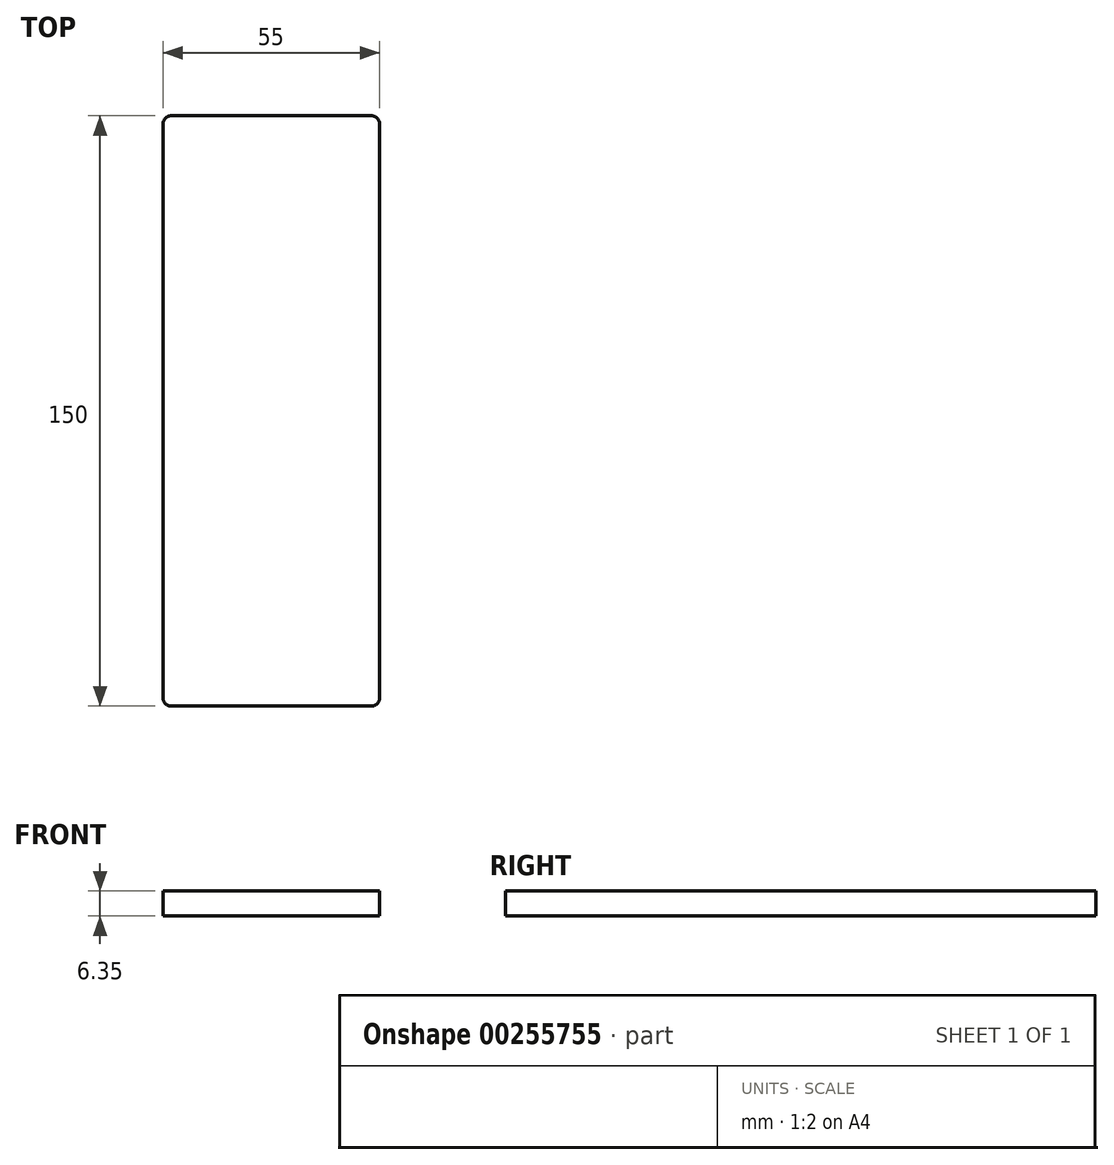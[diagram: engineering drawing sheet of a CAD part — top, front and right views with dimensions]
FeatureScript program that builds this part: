
annotation { "Feature Type Name" : "Feature", "Feature Type Description" : "" }
export const myFeature = defineFeature(function(context is Context, id is Id, definition is map)
    precondition{}
    {
        {
            var Q0;
            Q0=qCreatedBy(makeId("Top.planeOp"),FACE);
            var sketch = newSketch(context, id + "F0", { "sketchPlane" : qUnion([Q0])});
            skLineSegment(sketch, "E0.bottom", {"start": v(-26, 75) * mm, "end": v(29, 75) * mm});
            skLineSegment(sketch, "E0.top", {"start": v(-26, -75) * mm, "end": v(29, -75) * mm});
            skLineSegment(sketch, "E0.left", {"start": v(-26, 75) * mm, "end": v(-26, -75) * mm});
            skLineSegment(sketch, "E0.right", {"start": v(29, 75) * mm, "end": v(29, -75) * mm});
            skLineSegment(sketch, "E1", {"start": v(-18, 0) * mm, "end": v(18, 0) * mm, "construction": true});
            skSolve(sketch);
        }
        {
            var Q0;
            Q0=makeQuery(id+"F0.imprint","IMPRINT",FACE,{"disambiguationData":[TD([[makeQuery(id+"F0.imprint","IMPRINT",EDGE,{"derivedFrom":sQuery(id+"F0.wireOp",EDGE,"E0.bottom")}),-1.0]])]});
            extrude(context, id + "F1", {"entities" : qUnion([Q0]), "depth" : 6.35 * mm});
        }
        {
            var Q0;
            Q0=makeQuery(id+"F1.opExtrude","SWEPT_EDGE",EDGE,{"disambiguationData":[OSD([sQuery(id+"F0.wireOp",EDGE,"E0.top"),sQuery(id+"F0.wireOp",EDGE,"E0.left")])]});
            var Q1;
            Q1=makeQuery(id+"F1.opExtrude","SWEPT_EDGE",EDGE,{"disambiguationData":[OSD([sQuery(id+"F0.wireOp",EDGE,"E0.top"),sQuery(id+"F0.wireOp",EDGE,"E0.right")])]});
            var Q2;
            Q2=makeQuery(id+"F1.opExtrude","SWEPT_EDGE",EDGE,{"disambiguationData":[OSD([sQuery(id+"F0.wireOp",EDGE,"E0.bottom"),sQuery(id+"F0.wireOp",EDGE,"E0.right")])]});
            var Q3;
            Q3=makeQuery(id+"F1.opExtrude","SWEPT_EDGE",EDGE,{"disambiguationData":[OSD([sQuery(id+"F0.wireOp",EDGE,"E0.bottom"),sQuery(id+"F0.wireOp",EDGE,"E0.left")])]});
            fillet(context, id + "F2", {"entities" : qUnion([Q0, Q1, Q2, Q3]), "radius" : 2 * mm, "tangentPropagation" : true, "allowEdgeOverflow" : false});
        }
    });
